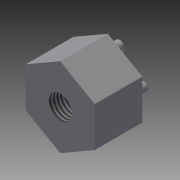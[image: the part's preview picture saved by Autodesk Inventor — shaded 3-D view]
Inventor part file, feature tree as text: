
AUTODESK INVENTOR PART (.ipt)
format: ipt  version: 2015 (Build 190159000, 159)  size: 95,232 bytes
history: native  units: mm
features: extrude x2, sketch x2, thread x1
ambient origin geometry x8: Origin, YZ Plane, XZ Plane, XY Plane, X Axis, Y Axis, Z Axis, Center Point
bodies: Solid1 (feature_tree)
feature tree (5):
  extrude  "Extrusion1"  Depth=20.0mm TaperAngle=0.0deg
  thread  "Thread1"  [1 undecoded]
  extrude  "Extrusion2"  Depth=5.0mm
  sketch  "Sketch1"  dims[d0=10.0mm d1=20.0mm d2=0.0mm d3=10.0mm d4=0.0mm]
  sketch  "Sketch2"  dims[d6=4.0mm d7=4.0mm d8=4.0mm d9=4.0mm d10=5.0mm d11=0.0mm]
note: 1 required parameter value undecoded (feature->parameter linkage not recoverable at this tier; creation-order binding heuristic only, values carry confidence <= 0.55)
